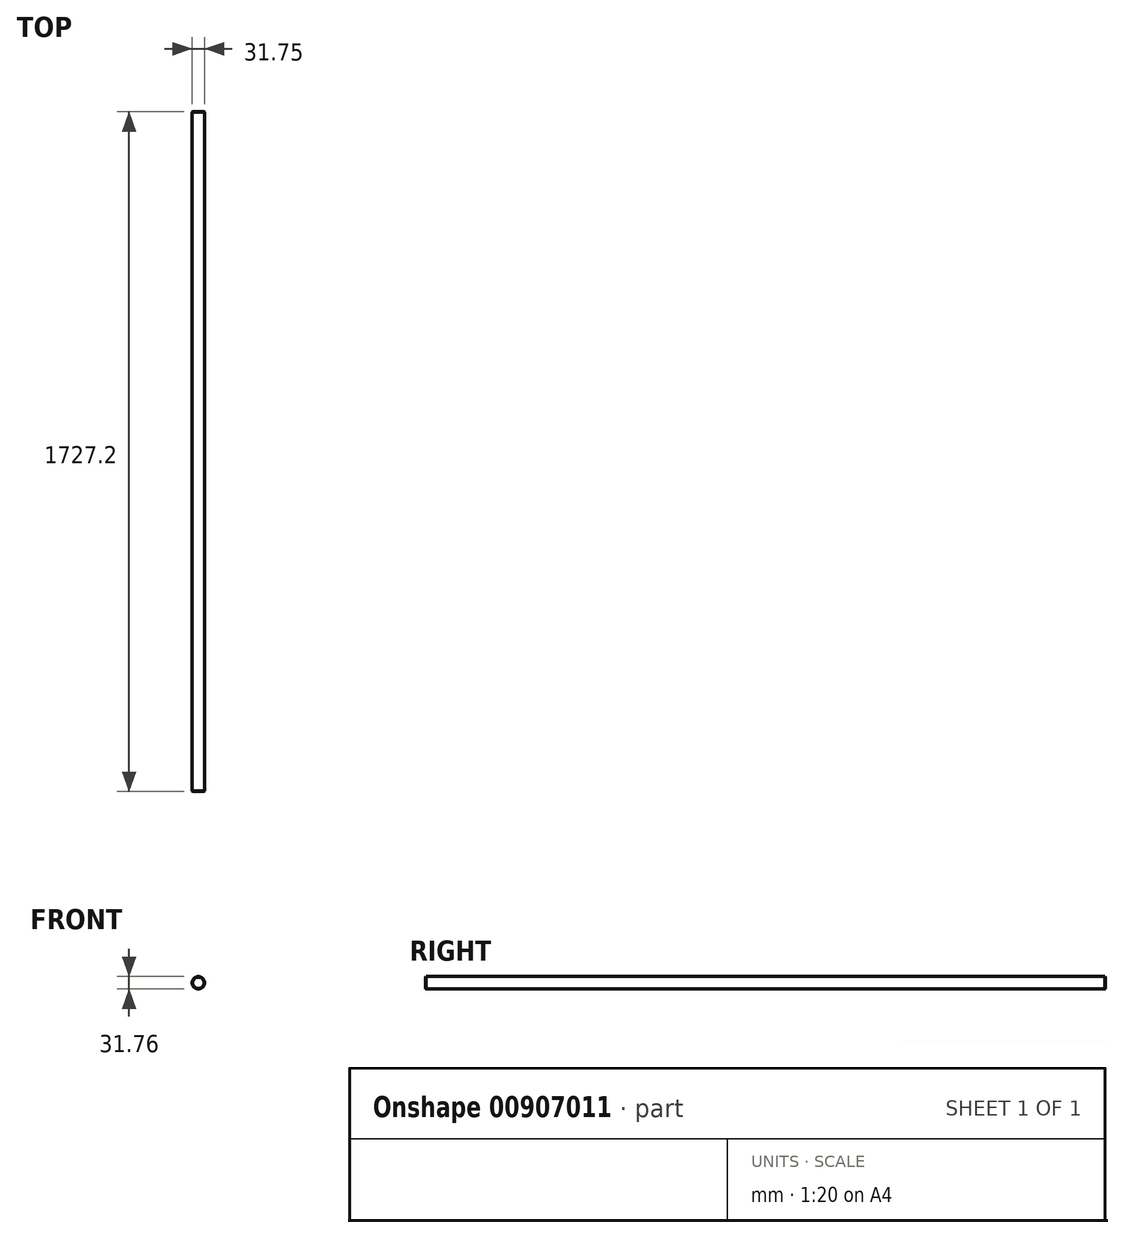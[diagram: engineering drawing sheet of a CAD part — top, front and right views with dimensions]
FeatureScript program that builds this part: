
annotation { "Feature Type Name" : "Feature", "Feature Type Description" : "" }
export const myFeature = defineFeature(function(context is Context, id is Id, definition is map)
    precondition{}
    {
        {
            var Q0;
            Q0=qCreatedBy(makeId("Front.planeOp"),FACE);
            var sketch = newSketch(context, id + "F0", { "sketchPlane" : qUnion([Q0])});
            skCircle(sketch, "E0", {"center": v(3.92, 0) * mm, "radius": 15.88 * mm});
            skSolve(sketch);
        }
        {
            var Q0;
            Q0=makeQuery(id+"F0.imprint","IMPRINT",FACE,{"disambiguationData":[TD([[makeQuery(id+"F0.imprint","IMPRINT",EDGE,{"derivedFrom":sQuery(id+"F0.wireOp",EDGE,"E0")}),1.0]])]});
            extrude(context, id + "F1", {"entities" : qUnion([Q0]), "depth" : 1727.2 * mm, "offsetDistance" : 25.4 * mm, "symmetric" : true});
        }
        {
            var Q0;
            Q0=makeQuery(id+"F1.opExtrude","CAP_EDGE",EDGE,{"disambiguationData":[OSD([sQuery(id+"F0.wireOp",EDGE,"E0")])],"isStart":false});
            var Q1;
            Q1=makeQuery(id+"F1.opExtrude","CAP_EDGE",EDGE,{"disambiguationData":[OSD([sQuery(id+"F0.wireOp",EDGE,"E0")])],"isStart":true});
            chamfer(context, id + "F2", {"entities" : qUnion([Q0, Q1]), "width" : 1.52 * mm, "tangentPropagation" : true});
        }
    });
